# Revit family: 0032003
name_source: partatom
category: Lighting Fixtures
revit_build: Autodesk Revit 2017 (Build: 20190507_1515(x64)
units: mm (PartAtom-declared; Revit-internal decimal feet)

## family parameters
Cut with Voids When Loaded = No
Host = Face
Light Source = Yes
OmniClass Number = 23.80.70.00
OmniClass Title = Lighting
Part Type = Normal
Room Calculation Point = No
Round Connector Dimension = Use Diameter
Shared = No

## types (2) — shared parameters
Apparent Load = 1 VA
Assembly Code = D5020200
AssetType = Fixed
ClassificationName = Uniclass2015
ClassificationValue = EF_70_80
Color Filter = 16777215
Default Elevation = 1219 mm
Dimming Lamp Color Temperature Shift = <None>
DocumentationLiterature = http://www.sylvania-lighting.com
ElectricShockClassification = Class II
Emit Shape Visible in Rendering = No
Emit from Circle Diameter = 610 mm
IfcExportAs = IfcLightFixtureType
IfcExportType = IfcLightFixtureType
ImpactProtectionIndex = IK02
IngressProtection = IP20
Keynote = 16500
Lamp = LED
LampColourRenderingIndex = 70
LampColourTemperature = 5000 K
LampNominalLuminous = 170 lm
LampsType = LED
LuminousEfficacy = 130.7 lm/W
Manufacturer = Feilo Sylvania
ManufacturerName = Feilo Sylvania
Material_1_SYL = <By Category>
Material_2_SYL = <By Category>
Material_3_SYL = <By Category>
Material_4_SYL = <By Category>
NominalDepth = 45 mm
NominalHeight = 45 mm
NominalLength = 150 mm
PowerConsumption = 1.3 W
PowerFactor = 0.4
Tilt Angle = -90.00°
Type Image = <None>
URL = http://www.sylvania-lighting.com
Voltage = 0 V
Weight = 5.4 kg
zero-valued in all types: Cost

## per-type parameters (varying)
| type | Description | Material | Model | ModelNumber | ModelReference | Name | Photometric Web File | TypeName |
| 0032002 ST E EM SPOT MT NM 3H OPEN  AREA | Recessed Spot Light used for Emergency application | pc polycarbonate housing | START eco Emergency Spot MT NM 3h Open Area | 0032002 | START eco Emergency Spot MT NM 3h Open Area | START eco Emergency Spot MT NM 3h Open Area | 0032002.ies | START eco Emergency Spot MT NM 3h Open Area |
| 0032003 ST E EM SPOT MT NM 3H CORRIDOR | Recessed Spot Light used for Emergency application Narrow beam for corridor application | pc polycarbonate housing, pc polycarbonate diffuser | START eco Emergency Spot MT NM 3h Corridor | 0032003 | START eco Emergency Spot MT NM 3h Corridor | START eco Emergency Spot MT NM 3h Corridor | 0032003.ies | START eco Emergency Spot MT NM 3h Corridor |

## geometry (parser evidence)
native form markers: Sweep x2
no freeform markers — native parametric forms only
